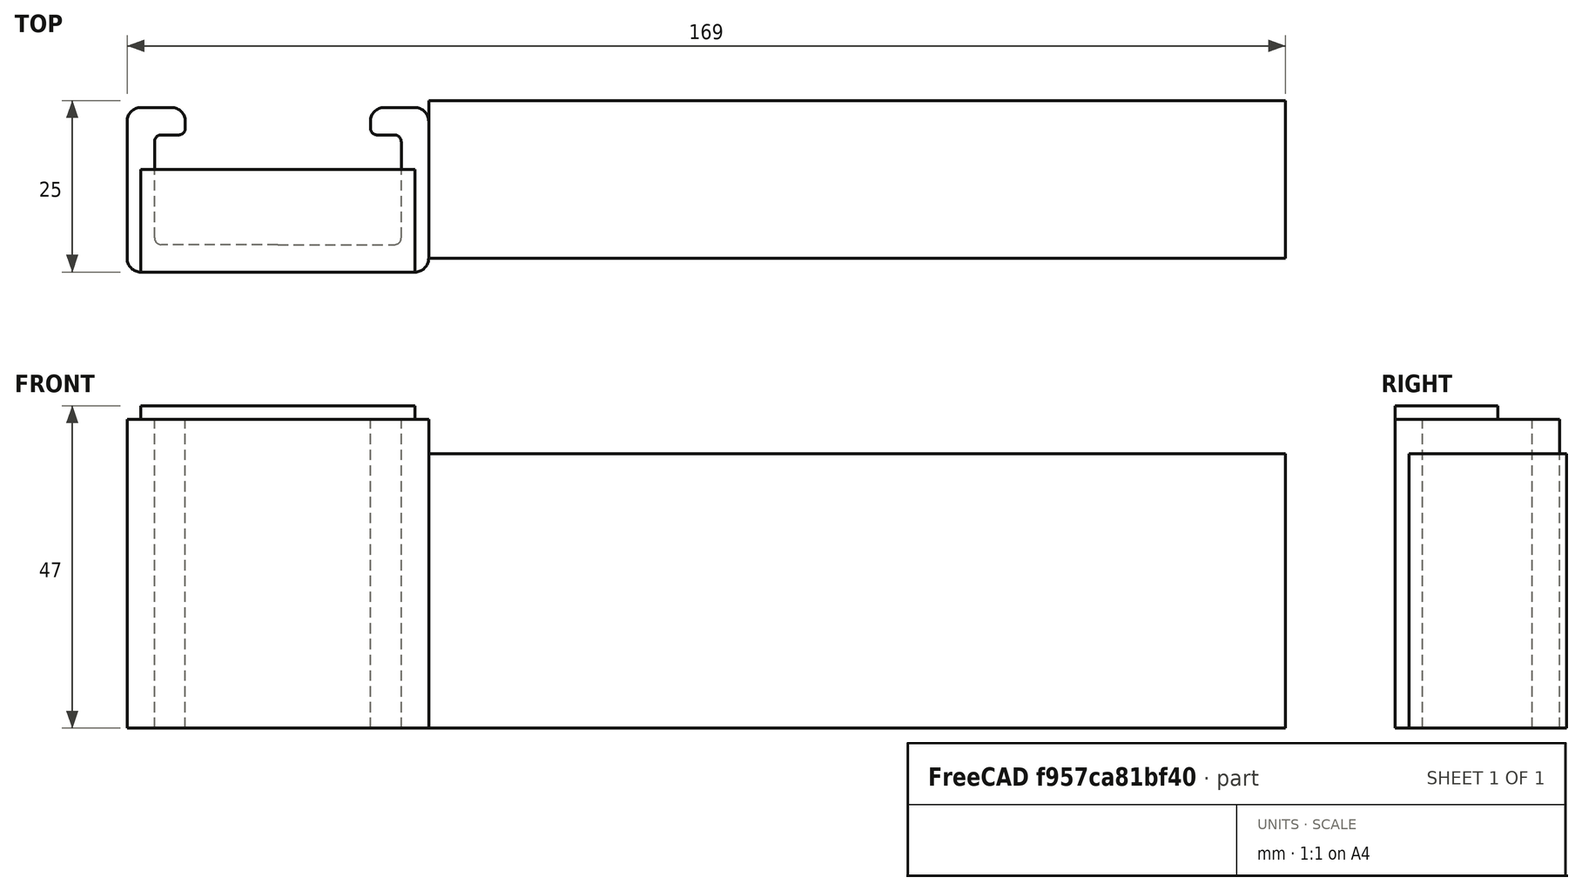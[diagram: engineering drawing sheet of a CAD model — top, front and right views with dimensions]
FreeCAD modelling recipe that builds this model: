
FCSTD DOCUMENT  (FreeCAD 0.20R24693 (Git))
Label: runout_mount
License: All rights reserved
LicenseURL: http://en.wikipedia.org/wiki/All_rights_reserved
objects: Sketcher::SketchObject×2, PartDesign::Pad×2, Part::Box×2, PartDesign::Body×1, Mesh::Feature×1
note: 9 computed .brp shape members not serialized (recipe doc carries the construction recipe); baked Part::Feature solids carry a one-line shape summary decoded from their .brp

FEATURE [Sketcher::SketchObject] Sketch
  FullyConstrained = true
  MapMode = 5
  Support = -> [XY_Plane]
  sketch-geometry (14):
    g0: LineSegment StartX=0 StartY=0 StartZ=0 EndX=-17 EndY=0 EndZ=0
    g1: LineSegment StartX=-18 StartY=1 StartZ=0 EndX=-18 EndY=15 EndZ=0
    g2: LineSegment StartX=-17 StartY=16 StartZ=0 EndX=-14.5 EndY=16 EndZ=0
    g3: LineSegment StartX=-13.5 StartY=17 StartZ=0 EndX=-13.5 EndY=18 EndZ=0
    g4: LineSegment StartX=-15.5 StartY=20 StartZ=0 EndX=-20 EndY=20 EndZ=0
    g5: LineSegment StartX=-22 StartY=18 StartZ=0 EndX=-22 EndY=-2 EndZ=0
    g6: LineSegment StartX=-20 StartY=-4 StartZ=0 EndX=0 EndY=-4 EndZ=0
    g7: ArcOfCircle CenterX=-20 CenterY=18 CenterZ=0 NormalX=0 NormalY=0 NormalZ=1 AngleXU=0 Radius=2 StartAngle=1.5708 EndAngle=3.14159
    g8: ArcOfCircle CenterX=-15.5 CenterY=18 CenterZ=0 NormalX=0 NormalY=0 NormalZ=1 AngleXU=0 Radius=2 StartAngle=4e-16 EndAngle=1.5708
    g9: ArcOfCircle CenterX=-14.5 CenterY=17 CenterZ=0 NormalX=0 NormalY=0 NormalZ=1 AngleXU=0 Radius=1 StartAngle=4.71239 EndAngle=6.28319
    g10: ArcOfCircle CenterX=-17 CenterY=15 CenterZ=0 NormalX=0 NormalY=0 NormalZ=1 AngleXU=0 Radius=1 StartAngle=1.5708 EndAngle=3.14159
    g11: ArcOfCircle CenterX=-17 CenterY=1 CenterZ=0 NormalX=0 NormalY=0 NormalZ=1 AngleXU=0 Radius=1 StartAngle=3.14159 EndAngle=4.71239
    g12: ArcOfCircle CenterX=-20 CenterY=-2 CenterZ=0 NormalX=0 NormalY=0 NormalZ=1 AngleXU=0 Radius=2 StartAngle=3.14159 EndAngle=4.71239
    g13: LineSegment StartX=0 StartY=-4 StartZ=0 EndX=0 EndY=0 EndZ=0
  constraints (36):
    c: PointOnObject(g0,g-2)
    c: Horizontal(g4)
    c: Horizontal(g2)
    c: Horizontal(g0)
    c: Horizontal(g6)
    c: Vertical(g5)
    c: Vertical(g1)
    c: Vertical(g3)
    c: Tangent(g5,g7) = -1.5708
    c: Tangent(g4,g7) = -1.5708
    c: Tangent(g4,g8) = -1.5708
    c: Tangent(g3,g8) = -1.5708
    c: Tangent(g3,g9) = -1.5708
    c: Tangent(g2,g9) = -1.5708
    c: Tangent(g2,g10) = 1.5708
    c: Tangent(g1,g10) = 1.5708
    c: Tangent(g1,g11) = 1.5708
    c: Tangent(g0,g11) = 1.5708
    c: Tangent(g6,g12) = -1.5708
    c: Tangent(g5,g12) = -1.5708
    c: Equal(g12,g7)
    c: Equal(g7,g8)
    c: Radius(g12) = 2
    c: Equal(g10,g11)
    c: Radius(g11) = 1
    c: DistanceY(g6,g0) = 4
    c: DistanceX(g5,g1) = 4
    c: DistanceX(g1,g0) = 18
    c: DistanceY(g2,g4) = 4
    c: DistanceY(g0,g2) = 16
    c: Equal(g9,g10)
    c: DistanceX(g3,g0) = 13.5
    c: DistanceY(g0,g-1) = 0
    c: DistanceX(g6,g0) = 0
    c: Coincident(g13,g6)
    c: Coincident(g13,g0)
FEATURE [Sketcher::SketchObject] MirroredSketch
  FullyConstrained = false
  sketch-geometry (14):
    g0: LineSegment StartX=0 StartY=0 StartZ=0 EndX=17 EndY=0 EndZ=0
    g1: LineSegment StartX=18 StartY=1 StartZ=0 EndX=18 EndY=15 EndZ=0
    g2: LineSegment StartX=17 StartY=16 StartZ=0 EndX=14.5 EndY=16 EndZ=0
    g3: LineSegment StartX=13.5 StartY=17 StartZ=0 EndX=13.5 EndY=18 EndZ=0
    g4: LineSegment StartX=15.5 StartY=20 StartZ=0 EndX=20 EndY=20 EndZ=0
    g5: LineSegment StartX=22 StartY=18 StartZ=0 EndX=22 EndY=-2 EndZ=0
    g6: LineSegment StartX=20 StartY=-4 StartZ=0 EndX=0 EndY=-4 EndZ=0
    g7: ArcOfCircle CenterX=20 CenterY=18 CenterZ=0 NormalX=0 NormalY=0 NormalZ=1 AngleXU=0 Radius=2 StartAngle=0 EndAngle=1.5708
    g8: ArcOfCircle CenterX=15.5 CenterY=18 CenterZ=0 NormalX=0 NormalY=0 NormalZ=1 AngleXU=0 Radius=2 StartAngle=1.5708 EndAngle=3.14159
    g9: ArcOfCircle CenterX=14.5 CenterY=17 CenterZ=0 NormalX=0 NormalY=0 NormalZ=1 AngleXU=0 Radius=1 StartAngle=3.14159 EndAngle=4.71239
    g10: ArcOfCircle CenterX=17 CenterY=15 CenterZ=0 NormalX=0 NormalY=0 NormalZ=1 AngleXU=0 Radius=1 StartAngle=0 EndAngle=1.5708
    g11: ArcOfCircle CenterX=17 CenterY=1 CenterZ=0 NormalX=0 NormalY=0 NormalZ=1 AngleXU=0 Radius=1 StartAngle=4.71239 EndAngle=6.28319
    g12: ArcOfCircle CenterX=20 CenterY=-2 CenterZ=0 NormalX=0 NormalY=0 NormalZ=1 AngleXU=0 Radius=2 StartAngle=4.71239 EndAngle=6.28319
    g13: LineSegment StartX=0 StartY=-4 StartZ=0 EndX=0 EndY=0 EndZ=0
  constraints (27):
    c: Horizontal(g4)
    c: Horizontal(g2)
    c: Horizontal(g0)
    c: Horizontal(g6)
    c: Vertical(g5)
    c: Vertical(g1)
    c: Vertical(g3)
    c: Tangent(g5,g7) = 1.5708
    c: Tangent(g4,g7) = 1.5708
    c: Tangent(g4,g8) = 1.5708
    c: Tangent(g3,g8) = 1.5708
    c: Tangent(g3,g9) = 1.5708
    c: Tangent(g2,g9) = 1.5708
    c: Tangent(g2,g10) = -1.5708
    c: Tangent(g1,g10) = -1.5708
    c: Tangent(g1,g11) = -1.5708
    c: Tangent(g0,g11) = -1.5708
    c: Tangent(g6,g12) = 1.5708
    c: Tangent(g5,g12) = 1.5708
    c: Equal(g12,g7)
    c: Equal(g7,g8)
    c: Radius(g12) = 2
    c: Equal(g10,g11)
    c: Radius(g11) = 1
    c: Equal(g9,g10)
    c: Coincident(g13,g6)
    c: Coincident(g13,g0)
FEATURE [PartDesign::Pad] Pad
  Direction = (0,0,1)
  Length = 45
  Length2 = 100
  Profile = -> Sketch
  Type = 0
FEATURE [PartDesign::Pad] Pad001
  BaseFeature = -> Pad
  Direction = (0,0,1)
  Length = 45
  Length2 = 100
  Profile = -> MirroredSketch
  Type = 0
FEATURE [PartDesign::Body] Body
  Group = -> [Sketch,MirroredSketch,Pad,Pad001]
  Origin = -> Origin
  Tip = -> Pad001
FEATURE [Mesh::Feature] _DPNFilHoldBrace  label="3DPNFilHoldBrace"
  Placement = pos=(147,22,-20) rot=(-0.57735,-0.57735,0.57735;2.0944rad)
FEATURE [Part::Box] Box  label="Cube"
  AttacherType = Attacher::AttachEngine3D
  Height = 40
  Length = 125
  Placement = pos=(22,-2,0) rot=(0,0,1;0rad)
  Width = 23
FEATURE [Part::Box] Box001  label="Cube001"
  AttacherType = Attacher::AttachEngine3D
  Height = 2
  Length = 40
  Placement = pos=(-20,-4,45) rot=(0,0,1;0rad)
  Width = 15
